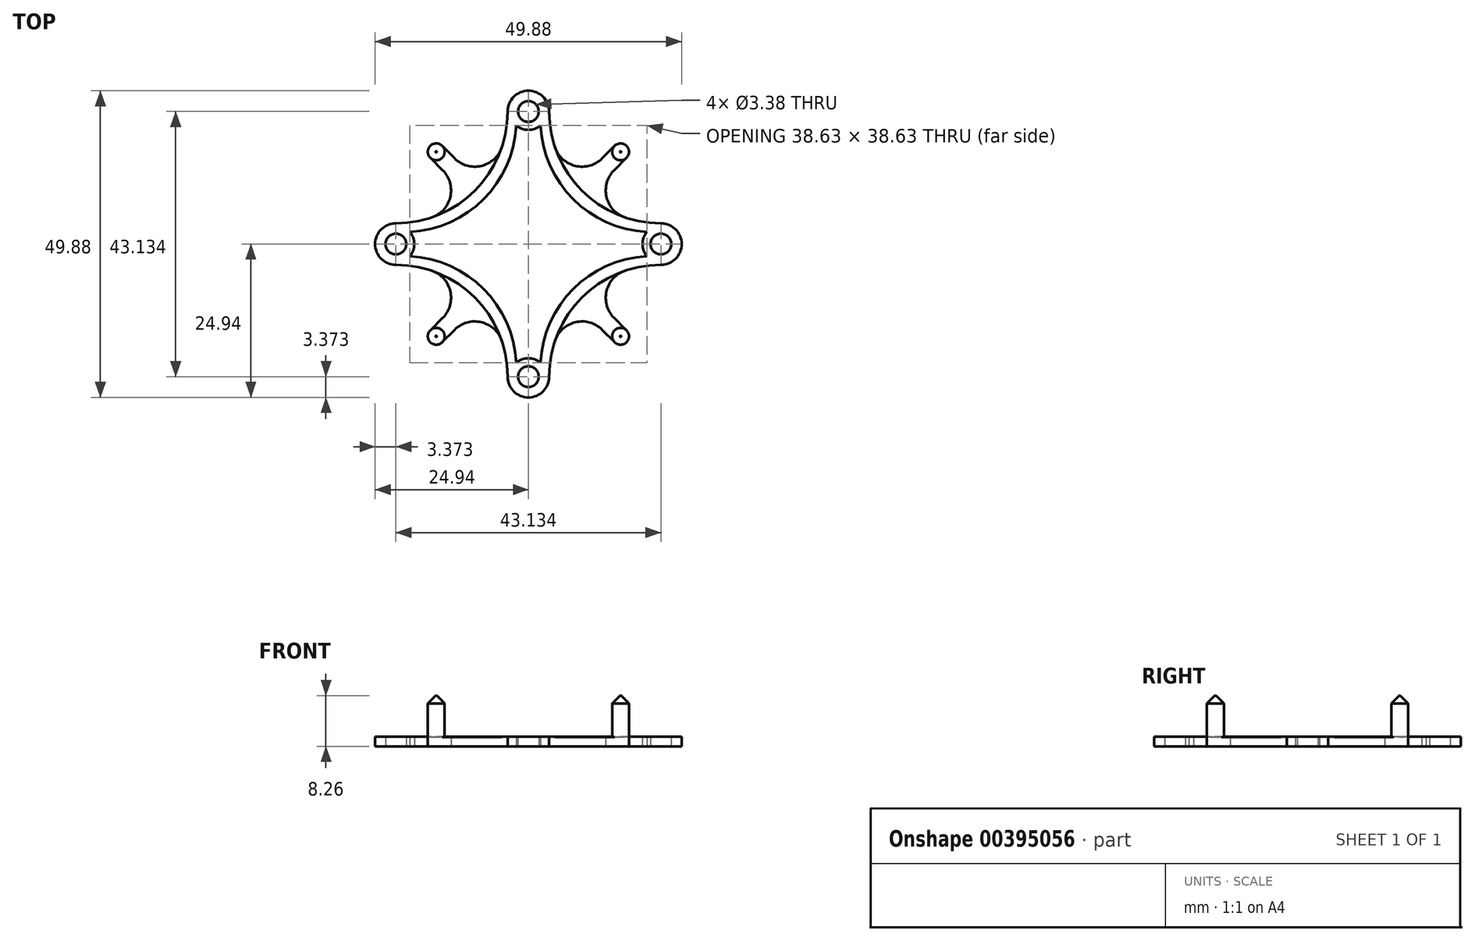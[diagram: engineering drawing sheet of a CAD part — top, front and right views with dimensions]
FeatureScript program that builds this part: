
annotation { "Feature Type Name" : "Feature", "Feature Type Description" : "" }
export const myFeature = defineFeature(function(context is Context, id is Id, definition is map)
    precondition{}
    {
        {
            var Q0;
            Q0=qCreatedBy(makeId("Top.planeOp"),FACE);
            var sketch = newSketch(context, id + "F0", { "sketchPlane" : qUnion([Q0])});
            skCircle(sketch, "E0", {"center": v(0, 21.57) * mm, "radius": 1.69 * mm});
            skCircle(sketch, "E1", {"center": v(-21.57, 0) * mm, "radius": 1.69 * mm});
            skCircle(sketch, "E2", {"center": v(0, -21.57) * mm, "radius": 1.69 * mm});
            skCircle(sketch, "E3", {"center": v(21.57, 0) * mm, "radius": 1.69 * mm});
            skLineSegment(sketch, "E4", {"start": v(0, 21.57) * mm, "end": v(0, -21.57) * mm, "construction": true});
            skLineSegment(sketch, "E5", {"start": v(21.57, 0) * mm, "end": v(-21.57, 0) * mm, "construction": true});
            skArc(sketch, "E6", {"start": v(3.38, 21.57) * mm, "mid": v(0, 24.94) * mm, "end": v(-3.38, 21.57) * mm});
            skArc(sketch, "E7", {"start": v(21.57, -3.38) * mm, "mid": v(24.94, 0) * mm, "end": v(21.57, 3.38) * mm});
            skArc(sketch, "E8", {"start": v(-3.38, -21.57) * mm, "mid": v(0, -24.94) * mm, "end": v(3.38, -21.57) * mm});
            skArc(sketch, "E9", {"start": v(-21.57, 3.38) * mm, "mid": v(-24.94, 0) * mm, "end": v(-21.57, -3.38) * mm});
            skArc(sketch, "E10", {"start": v(21.57, -3.38) * mm, "mid": v(8.7, -8.7) * mm, "end": v(3.38, -21.57) * mm});
            skArc(sketch, "E11", {"start": v(3.38, 21.57) * mm, "mid": v(8.7, 8.7) * mm, "end": v(21.57, 3.38) * mm});
            skArc(sketch, "E12", {"start": v(-21.57, 3.38) * mm, "mid": v(-8.7, 8.7) * mm, "end": v(-3.38, 21.57) * mm});
            skArc(sketch, "E13", {"start": v(-3.38, -21.57) * mm, "mid": v(-8.7, -8.7) * mm, "end": v(-21.57, -3.38) * mm});
            skArc(sketch, "E14", {"start": v(-1.98, 19.32) * mm, "mid": v(0, 18.57) * mm, "end": v(1.98, 19.32) * mm});
            skArc(sketch, "E15", {"start": v(-19.32, -1.98) * mm, "mid": v(-18.57, 0) * mm, "end": v(-19.32, 1.98) * mm});
            skArc(sketch, "E16", {"start": v(1.98, -19.32) * mm, "mid": v(0, -18.57) * mm, "end": v(-1.98, -19.32) * mm});
            skArc(sketch, "E17", {"start": v(19.32, 1.98) * mm, "mid": v(18.57, 0) * mm, "end": v(19.32, -1.98) * mm});
            skArc(sketch, "E18", {"start": v(19.32, -1.98) * mm, "mid": v(7.3, -7.3) * mm, "end": v(1.98, -19.32) * mm});
            skArc(sketch, "E19", {"start": v(1.98, 19.32) * mm, "mid": v(7.3, 7.3) * mm, "end": v(19.32, 1.98) * mm});
            skArc(sketch, "E20", {"start": v(-19.32, 1.98) * mm, "mid": v(-7.3, 7.3) * mm, "end": v(-1.98, 19.32) * mm});
            skArc(sketch, "E21", {"start": v(-1.98, -19.32) * mm, "mid": v(-7.3, -7.3) * mm, "end": v(-19.32, -1.98) * mm});
            skSolve(sketch);
        }
        {
            var Q0;
            Q0=makeQuery(id+"F0.imprint","IMPRINT",FACE,{"disambiguationData":[TD([[makeQuery(id+"F0.imprint","IMPRINT",EDGE,{"derivedFrom":sQuery(id+"F0.wireOp",EDGE,"E0")}),-1.0]])]});
            extrude(context, id + "F1", {"entities" : qUnion([Q0]), "depth" : 0.01 * mm});
        }
        {
            var Q0;
            Q0=qCreatedBy(makeId("Top.planeOp"),FACE);
            var sketch = newSketch(context, id + "F2", { "sketchPlane" : qUnion([Q0])});
            skLineSegment(sketch, "E22.bottom", {"start": v(15, -15) * mm, "end": v(-15, -15) * mm, "construction": true});
            skLineSegment(sketch, "E22.top", {"start": v(15, 15) * mm, "end": v(-15, 15) * mm, "construction": true});
            skLineSegment(sketch, "E22.left", {"start": v(15, -15) * mm, "end": v(15, 15) * mm, "construction": true});
            skLineSegment(sketch, "E22.right", {"start": v(-15, -15) * mm, "end": v(-15, 15) * mm, "construction": true});
            skPoint(sketch, "E22.middle", {"position": v(0, 0) * mm});
            skCircle(sketch, "E23", {"center": v(15, 15) * mm, "radius": 1.37 * mm});
            skCircle(sketch, "E24", {"center": v(15, -15) * mm, "radius": 1.37 * mm});
            skCircle(sketch, "E25", {"center": v(-15, 15) * mm, "radius": 1.37 * mm});
            skCircle(sketch, "E26", {"center": v(-15, -15) * mm, "radius": 1.37 * mm});
            skSolve(sketch);
        }
        {
            var Q0;
            Q0=makeQuery(id+"F2.imprint","IMPRINT",FACE,{"disambiguationData":[TD([[makeQuery(id+"F2.imprint","IMPRINT",EDGE,{"derivedFrom":sQuery(id+"F2.wireOp",EDGE,"E23")}),1.0]])]});
            var Q1;
            Q1=makeQuery(id+"F2.imprint","IMPRINT",FACE,{"disambiguationData":[TD([[makeQuery(id+"F2.imprint","IMPRINT",EDGE,{"derivedFrom":sQuery(id+"F2.wireOp",EDGE,"E25")}),1.0]])]});
            var Q2;
            Q2=makeQuery(id+"F2.imprint","IMPRINT",FACE,{"disambiguationData":[TD([[makeQuery(id+"F2.imprint","IMPRINT",EDGE,{"derivedFrom":sQuery(id+"F2.wireOp",EDGE,"E24")}),1.0]])]});
            var Q3;
            Q3=makeQuery(id+"F2.imprint","IMPRINT",FACE,{"disambiguationData":[TD([[makeQuery(id+"F2.imprint","IMPRINT",EDGE,{"derivedFrom":sQuery(id+"F2.wireOp",EDGE,"E26")}),1.0]])]});
            extrude(context, id + "F3", {"entities" : qUnion([Q0, Q1, Q2, Q3]), "depth" : 8.25 * mm});
        }
        {
            var Q0;
            Q0=qCreatedBy(makeId("Top.planeOp"),FACE);
            var sketch = newSketch(context, id + "F4", { "sketchPlane" : qUnion([Q0])});
            skLineSegment(sketch, "E27", {"start": v(-14.03, 15.97) * mm, "end": v(-6.36, 8.3) * mm});
            skLineSegment(sketch, "E28", {"start": v(-6.36, 8.3) * mm, "end": v(-8.3, 6.36) * mm});
            skLineSegment(sketch, "E29", {"start": v(-8.3, 6.36) * mm, "end": v(-15.97, 14.03) * mm});
            skLineSegment(sketch, "E30", {"start": v(-15.97, 14.03) * mm, "end": v(-14.03, 15.97) * mm});
            skLineSegment(sketch, "E31", {"start": v(14.03, 15.97) * mm, "end": v(15.97, 14.03) * mm});
            skLineSegment(sketch, "E32", {"start": v(15.97, 14.03) * mm, "end": v(8.3, 6.36) * mm});
            skLineSegment(sketch, "E33", {"start": v(8.3, 6.36) * mm, "end": v(6.36, 8.3) * mm});
            skLineSegment(sketch, "E34", {"start": v(6.36, 8.3) * mm, "end": v(14.03, 15.97) * mm});
            skLineSegment(sketch, "E35", {"start": v(8.3, -6.36) * mm, "end": v(15.97, -14.03) * mm});
            skLineSegment(sketch, "E36", {"start": v(15.97, -14.03) * mm, "end": v(14.03, -15.97) * mm});
            skLineSegment(sketch, "E37", {"start": v(14.03, -15.97) * mm, "end": v(6.36, -8.3) * mm});
            skLineSegment(sketch, "E38", {"start": v(6.36, -8.3) * mm, "end": v(8.3, -6.36) * mm});
            skLineSegment(sketch, "E39", {"start": v(-15.97, -14.03) * mm, "end": v(-14.03, -15.97) * mm});
            skLineSegment(sketch, "E40", {"start": v(-14.03, -15.97) * mm, "end": v(-6.36, -8.3) * mm});
            skLineSegment(sketch, "E41", {"start": v(-6.36, -8.3) * mm, "end": v(-8.3, -6.36) * mm});
            skLineSegment(sketch, "E42", {"start": v(-8.3, -6.36) * mm, "end": v(-15.97, -14.03) * mm});
            skLineSegment(sketch, "E43", {"start": v(-7.33, -7.33) * mm, "end": v(0, 0) * mm, "construction": true});
            skLineSegment(sketch, "E44", {"start": v(0, 0) * mm, "end": v(7.33, 7.33) * mm, "construction": true});
            skLineSegment(sketch, "E45", {"start": v(-7.33, 7.33) * mm, "end": v(0, 0) * mm, "construction": true});
            skLineSegment(sketch, "E46", {"start": v(7.33, -7.33) * mm, "end": v(0, 0) * mm, "construction": true});
            skSolve(sketch);
        }
        {
            var Q0;
            Q0=makeQuery(id+"F4.imprint","IMPRINT",FACE,{"disambiguationData":[TD([[makeQuery(id+"F4.imprint","IMPRINT",EDGE,{"derivedFrom":sQuery(id+"F4.wireOp",EDGE,"E31")}),-1.0]])]});
            var Q1;
            Q1=makeQuery(id+"F4.imprint","IMPRINT",FACE,{"disambiguationData":[TD([[makeQuery(id+"F4.imprint","IMPRINT",EDGE,{"derivedFrom":sQuery(id+"F4.wireOp",EDGE,"E27")}),-1.0]])]});
            var Q2;
            Q2=makeQuery(id+"F4.imprint","IMPRINT",FACE,{"disambiguationData":[TD([[makeQuery(id+"F4.imprint","IMPRINT",EDGE,{"derivedFrom":sQuery(id+"F4.wireOp",EDGE,"E35")}),-1.0]])]});
            var Q3;
            Q3=makeQuery(id+"F4.imprint","IMPRINT",FACE,{"disambiguationData":[TD([[makeQuery(id+"F4.imprint","IMPRINT",EDGE,{"derivedFrom":sQuery(id+"F4.wireOp",EDGE,"E39")}),1.0]])]});
            var Q4;
            Q4=makeQuery(id+"F1.opExtrude","CAP_FACE",FACE,{"disambiguationData":[OSD([sQuery(id+"F0.wireOp",EDGE,"E0"),sQuery(id+"F0.wireOp",EDGE,"E1"),sQuery(id+"F0.wireOp",EDGE,"E2"),sQuery(id+"F0.wireOp",EDGE,"E3"),sQuery(id+"F0.wireOp",EDGE,"E6"),sQuery(id+"F0.wireOp",EDGE,"E7"),sQuery(id+"F0.wireOp",EDGE,"E8"),sQuery(id+"F0.wireOp",EDGE,"E9"),sQuery(id+"F0.wireOp",EDGE,"E10"),sQuery(id+"F0.wireOp",EDGE,"E11"),sQuery(id+"F0.wireOp",EDGE,"E12"),sQuery(id+"F0.wireOp",EDGE,"E13"),sQuery(id+"F0.wireOp",EDGE,"E14"),sQuery(id+"F0.wireOp",EDGE,"E15"),sQuery(id+"F0.wireOp",EDGE,"E16"),sQuery(id+"F0.wireOp",EDGE,"E17"),sQuery(id+"F0.wireOp",EDGE,"E18"),sQuery(id+"F0.wireOp",EDGE,"E19"),sQuery(id+"F0.wireOp",EDGE,"E20"),sQuery(id+"F0.wireOp",EDGE,"E21")])],"isStart":false});
            extrude(context, id + "F5", {"entities" : qUnion([Q0, Q1, Q2, Q3, Q4]), "operationType" : NewBodyOperationType.ADD, "depth" : 1.52 * mm});
        }
        {
            var Q0;
            {var subQ0=sQuery(id+"F0.wireOp",EDGE,"E10");Q0=makeQuery(id+"F5.boolean.opBoolean","INTERSECT",EDGE,{"derivedFrom":[makeQuery(id+"F1.opExtrude","SWEPT_FACE",FACE,{"disambiguationData":[OSD([subQ0])]}),makeQuery(id+"F5.opExtrude","SWEPT_FACE",FACE,{"disambiguationData":[OSD([subQ0])]}),makeQuery(id+"F5.opExtrude","SWEPT_FACE",FACE,{"disambiguationData":[OSD([sQuery(id+"F4.wireOp",EDGE,"E37")])]})]});}
            var Q1;
            {var subQ0=sQuery(id+"F0.wireOp",EDGE,"E10");Q1=makeQuery(id+"F5.boolean.opBoolean","INTERSECT",EDGE,{"derivedFrom":[makeQuery(id+"F1.opExtrude","SWEPT_FACE",FACE,{"disambiguationData":[OSD([subQ0])]}),makeQuery(id+"F5.opExtrude","SWEPT_FACE",FACE,{"disambiguationData":[OSD([subQ0])]}),makeQuery(id+"F5.opExtrude","SWEPT_FACE",FACE,{"disambiguationData":[OSD([sQuery(id+"F4.wireOp",EDGE,"E35")])]})]});}
            var Q2;
            {var subQ0=sQuery(id+"F0.wireOp",EDGE,"E11");Q2=makeQuery(id+"F5.boolean.opBoolean","INTERSECT",EDGE,{"derivedFrom":[makeQuery(id+"F1.opExtrude","SWEPT_FACE",FACE,{"disambiguationData":[OSD([subQ0])]}),makeQuery(id+"F5.opExtrude","SWEPT_FACE",FACE,{"disambiguationData":[OSD([subQ0])]}),makeQuery(id+"F5.opExtrude","SWEPT_FACE",FACE,{"disambiguationData":[OSD([sQuery(id+"F4.wireOp",EDGE,"E32")])]})]});}
            var Q3;
            {var subQ0=sQuery(id+"F0.wireOp",EDGE,"E11");Q3=makeQuery(id+"F5.boolean.opBoolean","INTERSECT",EDGE,{"derivedFrom":[makeQuery(id+"F1.opExtrude","SWEPT_FACE",FACE,{"disambiguationData":[OSD([subQ0])]}),makeQuery(id+"F5.opExtrude","SWEPT_FACE",FACE,{"disambiguationData":[OSD([subQ0])]}),makeQuery(id+"F5.opExtrude","SWEPT_FACE",FACE,{"disambiguationData":[OSD([sQuery(id+"F4.wireOp",EDGE,"E34")])]})]});}
            var Q4;
            {var subQ0=sQuery(id+"F0.wireOp",EDGE,"E12");Q4=makeQuery(id+"F5.boolean.opBoolean","INTERSECT",EDGE,{"derivedFrom":[makeQuery(id+"F1.opExtrude","SWEPT_FACE",FACE,{"disambiguationData":[OSD([subQ0])]}),makeQuery(id+"F5.opExtrude","SWEPT_FACE",FACE,{"disambiguationData":[OSD([subQ0])]}),makeQuery(id+"F5.opExtrude","SWEPT_FACE",FACE,{"disambiguationData":[OSD([sQuery(id+"F4.wireOp",EDGE,"E27")])]})]});}
            var Q5;
            {var subQ0=sQuery(id+"F0.wireOp",EDGE,"E12");Q5=makeQuery(id+"F5.boolean.opBoolean","INTERSECT",EDGE,{"derivedFrom":[makeQuery(id+"F1.opExtrude","SWEPT_FACE",FACE,{"disambiguationData":[OSD([subQ0])]}),makeQuery(id+"F5.opExtrude","SWEPT_FACE",FACE,{"disambiguationData":[OSD([subQ0])]}),makeQuery(id+"F5.opExtrude","SWEPT_FACE",FACE,{"disambiguationData":[OSD([sQuery(id+"F4.wireOp",EDGE,"E29")])]})]});}
            var Q6;
            {var subQ0=sQuery(id+"F0.wireOp",EDGE,"E13");Q6=makeQuery(id+"F5.boolean.opBoolean","INTERSECT",EDGE,{"derivedFrom":[makeQuery(id+"F1.opExtrude","SWEPT_FACE",FACE,{"disambiguationData":[OSD([subQ0])]}),makeQuery(id+"F5.opExtrude","SWEPT_FACE",FACE,{"disambiguationData":[OSD([subQ0])]}),makeQuery(id+"F5.opExtrude","SWEPT_FACE",FACE,{"disambiguationData":[OSD([sQuery(id+"F4.wireOp",EDGE,"E42")])]})]});}
            var Q7;
            {var subQ0=sQuery(id+"F0.wireOp",EDGE,"E13");Q7=makeQuery(id+"F5.boolean.opBoolean","INTERSECT",EDGE,{"derivedFrom":[makeQuery(id+"F1.opExtrude","SWEPT_FACE",FACE,{"disambiguationData":[OSD([subQ0])]}),makeQuery(id+"F5.opExtrude","SWEPT_FACE",FACE,{"disambiguationData":[OSD([subQ0])]}),makeQuery(id+"F5.opExtrude","SWEPT_FACE",FACE,{"disambiguationData":[OSD([sQuery(id+"F4.wireOp",EDGE,"E40")])]})]});}
            fillet(context, id + "F6", {"entities" : qUnion([Q0, Q1, Q2, Q3, Q4, Q5, Q6, Q7]), "radius" : 4.64 * mm, "tangentPropagation" : true, "allowEdgeOverflow" : false});
        }
        {
            var Q0;
            Q0=makeQuery(id+"F3.opExtrude","CAP_EDGE",EDGE,{"disambiguationData":[OSD([sQuery(id+"F2.wireOp",EDGE,"E25")])],"isStart":false});
            var Q1;
            Q1=makeQuery(id+"F3.opExtrude","CAP_EDGE",EDGE,{"disambiguationData":[OSD([sQuery(id+"F2.wireOp",EDGE,"E23")])],"isStart":false});
            var Q2;
            Q2=makeQuery(id+"F3.opExtrude","CAP_EDGE",EDGE,{"disambiguationData":[OSD([sQuery(id+"F2.wireOp",EDGE,"E24")])],"isStart":false});
            var Q3;
            Q3=makeQuery(id+"F3.opExtrude","CAP_EDGE",EDGE,{"disambiguationData":[OSD([sQuery(id+"F2.wireOp",EDGE,"E26")])],"isStart":false});
            chamfer(context, id + "F7", {"entities" : qUnion([Q0, Q1, Q2, Q3]), "width" : 1.27 * mm, "tangentPropagation" : true});
        }
    });
